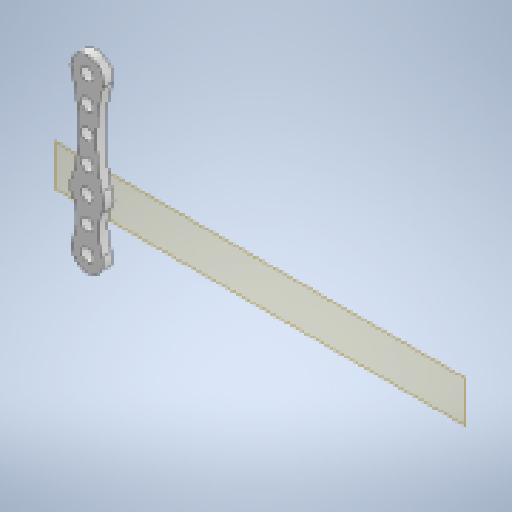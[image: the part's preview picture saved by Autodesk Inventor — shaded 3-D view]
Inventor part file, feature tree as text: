
AUTODESK INVENTOR PART (.ipt)
format: ipt  version: 2024.1 (Build 281209000, 209)  size: 185,344 bytes
history: native  units: mm
features: other x4, plane x1, extrude x1, sketch x1, reference x1
ambient origin geometry x8: Origin, YZ Plane, XZ Plane, XY Plane, X Axis, Y Axis, Z Axis, Center Point
bodies: Body1 (feature_tree)
feature tree (8):
  other  "see-saw-arm-1"
  plane  "Work Plane1"
  extrude  "Extrusion1"  Depth=2.5mm
  sketch  "Sketch1"  dims[d0=3.0mm d1=9.2mm d6=30.0mm d8=7.0mm d9=50.0mm d11=7.0mm d16=2.5mm d17=0.0mm d18=2.4mm d19=3.0mm d20=3.0mm d21=2.4mm]
  reference  "Reference1"
  other  "<userpath>\Documents\0004-CAD\3D-cad-main\the-artifact\artifact-assembly.iam"
  other  "artifact-assembly.iam"
  other  "anchor-point:1"
